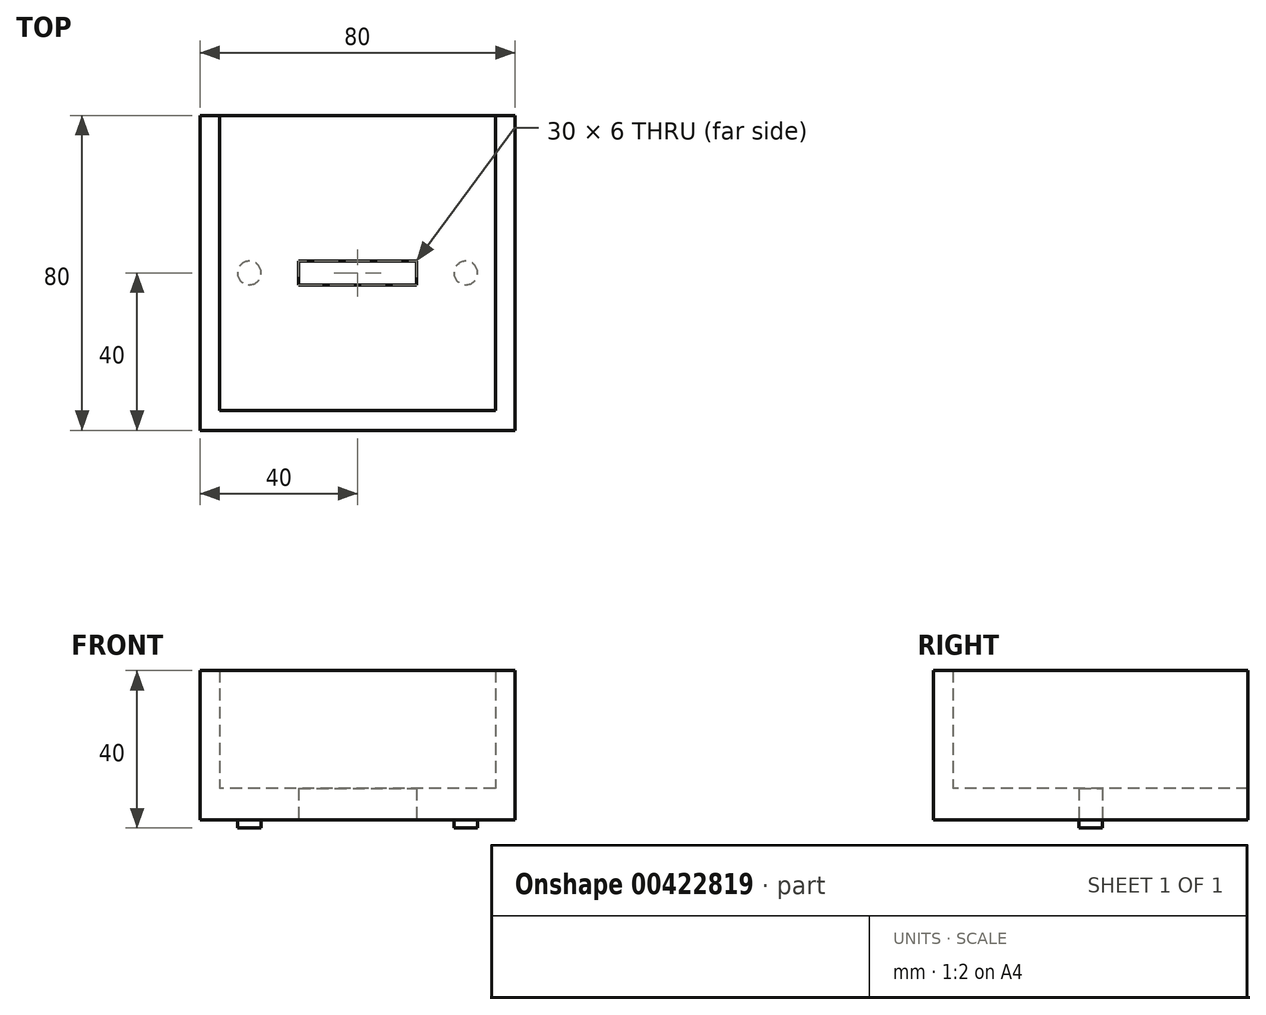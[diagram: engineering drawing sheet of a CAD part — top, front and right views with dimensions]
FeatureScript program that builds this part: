
annotation { "Feature Type Name" : "Feature", "Feature Type Description" : "" }
export const myFeature = defineFeature(function(context is Context, id is Id, definition is map)
    precondition{}
    {
        {
            var Q0;
            Q0=qCreatedBy(makeId("Top.planeOp"),FACE);
            var sketch = newSketch(context, id + "F0", { "sketchPlane" : qUnion([Q0])});
            skLineSegment(sketch, "E0.bottom", {"start": v(0, 0) * mm, "end": v(-80, 0) * mm});
            skLineSegment(sketch, "E0.top", {"start": v(0, 80) * mm, "end": v(-80, 80) * mm});
            skLineSegment(sketch, "E0.left", {"start": v(0, 0) * mm, "end": v(0, 80) * mm});
            skLineSegment(sketch, "E0.right", {"start": v(-80, 0) * mm, "end": v(-80, 80) * mm});
            skLineSegment(sketch, "E1.bottom", {"start": v(-55, 37) * mm, "end": v(-25, 37) * mm});
            skLineSegment(sketch, "E1.top", {"start": v(-55, 43) * mm, "end": v(-25, 43) * mm});
            skLineSegment(sketch, "E1.left", {"start": v(-55, 37) * mm, "end": v(-55, 43) * mm});
            skLineSegment(sketch, "E1.right", {"start": v(-25, 37) * mm, "end": v(-25, 43) * mm});
            skSolve(sketch);
        }
        {
            var Q0;
            Q0=makeQuery(id+"F0.imprint","IMPRINT",FACE,{"disambiguationData":[TD([[makeQuery(id+"F0.imprint","IMPRINT",EDGE,{"derivedFrom":sQuery(id+"F0.wireOp",EDGE,"E0.bottom")}),-1.0]])]});
            extrude(context, id + "F1", {"entities" : qUnion([Q0]), "depth" : 8 * mm});
        }
        {
            var Q0;
            Q0=makeQuery(id+"F1.opExtrude","CAP_FACE",FACE,{"disambiguationData":[OSD([sQuery(id+"F0.wireOp",EDGE,"E0.bottom"),sQuery(id+"F0.wireOp",EDGE,"E0.top"),sQuery(id+"F0.wireOp",EDGE,"E0.left"),sQuery(id+"F0.wireOp",EDGE,"E0.right"),sQuery(id+"F0.wireOp",EDGE,"E1.bottom"),sQuery(id+"F0.wireOp",EDGE,"E1.top"),sQuery(id+"F0.wireOp",EDGE,"E1.left"),sQuery(id+"F0.wireOp",EDGE,"E1.right")])],"isStart":false});
            var sketch = newSketch(context, id + "F2", { "sketchPlane" : qUnion([Q0])});
            skLineSegment(sketch, "E2.bottom", {"start": v(-80, 0) * mm, "end": v(-80, 0) * mm});
            skLineSegment(sketch, "E2.top", {"start": v(-80, 80) * mm, "end": v(-80, 80) * mm});
            skLineSegment(sketch, "E2.left", {"start": v(-80, 0) * mm, "end": v(-80, 80) * mm});
            skLineSegment(sketch, "E2.right", {"start": v(-80, 0) * mm, "end": v(-80, 80) * mm});
            skLineSegment(sketch, "E3.bottom", {"start": v(-80, 80) * mm, "end": v(-75, 80) * mm});
            skLineSegment(sketch, "E3.top", {"start": v(-80, 0) * mm, "end": v(-75, 0) * mm});
            skLineSegment(sketch, "E3.left", {"start": v(-80, 80) * mm, "end": v(-80, 0) * mm});
            skLineSegment(sketch, "E3.right", {"start": v(-75, 80) * mm, "end": v(-75, 0) * mm});
            skLineSegment(sketch, "E4.bottom", {"start": v(0, 0) * mm, "end": v(0, 0) * mm});
            skLineSegment(sketch, "E4.top", {"start": v(0, 80) * mm, "end": v(0, 80) * mm});
            skLineSegment(sketch, "E4.left", {"start": v(0, 0) * mm, "end": v(0, 80) * mm});
            skLineSegment(sketch, "E4.right", {"start": v(0, 0) * mm, "end": v(0, 80) * mm});
            skLineSegment(sketch, "E5.bottom", {"start": v(0, 80) * mm, "end": v(-5, 80) * mm});
            skLineSegment(sketch, "E5.top", {"start": v(0, 0) * mm, "end": v(-5, 0) * mm});
            skLineSegment(sketch, "E5.left", {"start": v(0, 80) * mm, "end": v(0, 0) * mm});
            skLineSegment(sketch, "E5.right", {"start": v(-5, 80) * mm, "end": v(-5, 0) * mm});
            skLineSegment(sketch, "E6.bottom", {"start": v(-75, 0) * mm, "end": v(-5, 0) * mm});
            skLineSegment(sketch, "E6.top", {"start": v(-75, 5) * mm, "end": v(-5, 5) * mm});
            skLineSegment(sketch, "E6.left", {"start": v(-75, 0) * mm, "end": v(-75, 5) * mm});
            skLineSegment(sketch, "E6.right", {"start": v(-5, 0) * mm, "end": v(-5, 5) * mm});
            skSolve(sketch);
        }
        {
            var Q0;
            Q0 = qSketchRegion(id + "F2", true);
            extrude(context, id + "F3", {"entities" : qUnion([Q0]), "operationType" : NewBodyOperationType.ADD, "depth" : 30 * mm});
        }
        {
            var Q0;
            Q0=makeQuery(id+"F1.opExtrude","CAP_FACE",FACE,{"disambiguationData":[OSD([sQuery(id+"F0.wireOp",EDGE,"E0.bottom"),sQuery(id+"F0.wireOp",EDGE,"E0.top"),sQuery(id+"F0.wireOp",EDGE,"E0.left"),sQuery(id+"F0.wireOp",EDGE,"E0.right"),sQuery(id+"F0.wireOp",EDGE,"E1.bottom"),sQuery(id+"F0.wireOp",EDGE,"E1.top"),sQuery(id+"F0.wireOp",EDGE,"E1.left"),sQuery(id+"F0.wireOp",EDGE,"E1.right")])],"isStart":true});
            var sketch = newSketch(context, id + "F4", { "sketchPlane" : qUnion([Q0])});
            skPoint(sketch, "E7", {"position": v(-12.5, -40) * mm});
            skPoint(sketch, "E7.positionSnap0", {"position": v(-25, -40) * mm});
            skPoint(sketch, "E8", {"position": v(-67.5, -40) * mm});
            skPoint(sketch, "E8.positionSnap0", {"position": v(-55, -40) * mm});
            skCircle(sketch, "E9", {"center": v(-12.5, -40) * mm, "radius": 3 * mm});
            skCircle(sketch, "E10", {"center": v(-67.5, -40) * mm, "radius": 3 * mm});
            skSolve(sketch);
        }
        {
            var Q0;
            Q0=makeQuery(id+"F4.imprint","IMPRINT",FACE,{"disambiguationData":[TD([[makeQuery(id+"F4.imprint","IMPRINT",EDGE,{"derivedFrom":sQuery(id+"F4.wireOp",EDGE,"E10")}),1.0]])]});
            var Q1;
            Q1=makeQuery(id+"F4.imprint","IMPRINT",FACE,{"disambiguationData":[TD([[makeQuery(id+"F4.imprint","IMPRINT",EDGE,{"derivedFrom":sQuery(id+"F4.wireOp",EDGE,"E9")}),1.0]])]});
            extrude(context, id + "F5", {"entities" : qUnion([Q0, Q1]), "operationType" : NewBodyOperationType.ADD, "depth" : 2 * mm});
        }
    });
